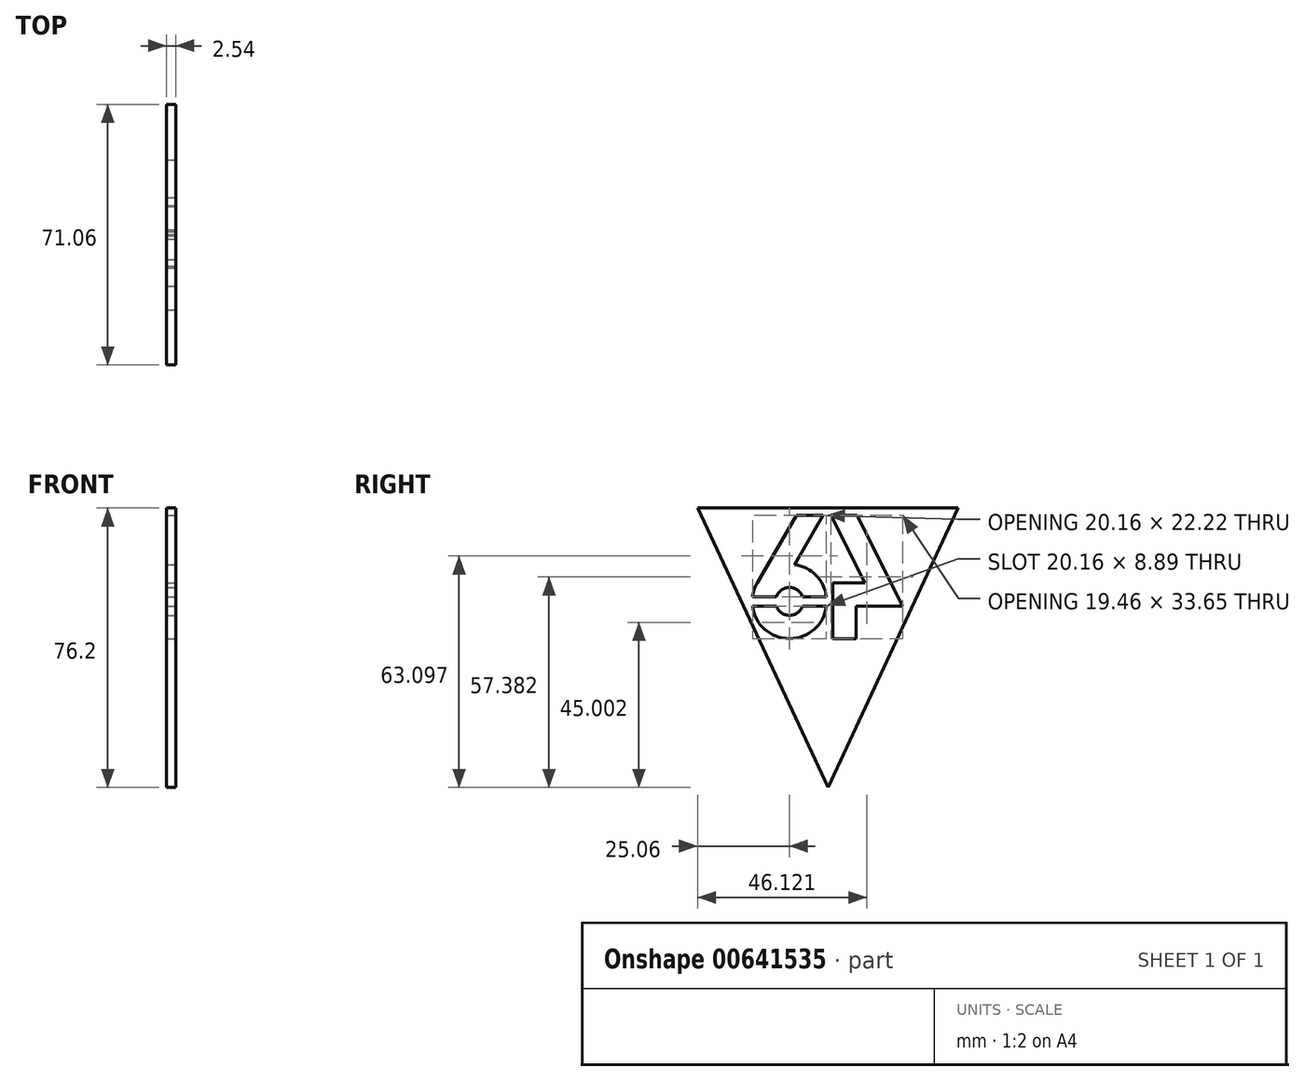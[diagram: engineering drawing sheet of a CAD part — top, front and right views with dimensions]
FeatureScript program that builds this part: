
annotation { "Feature Type Name" : "Feature", "Feature Type Description" : "" }
export const myFeature = defineFeature(function(context is Context, id is Id, definition is map)
    precondition{}
    {
        {
            var Q0;
            Q0=qCreatedBy(makeId("Right.planeOp"),FACE);
            var sketch = newSketch(context, id + "F0", { "sketchPlane" : qUnion([Q0])});
            skLineSegment(sketch, "E0", {"start": v(-35.53, 0) * mm, "end": v(35.53, 0) * mm});
            skLineSegment(sketch, "E1", {"start": v(35.53, 0) * mm, "end": v(0, -76.2) * mm});
            skLineSegment(sketch, "E2", {"start": v(0, -76.2) * mm, "end": v(-35.53, 0) * mm});
            skLineSegment(sketch, "E3", {"start": v(0, -76.2) * mm, "end": v(0, 0) * mm});
            skLineSegment(sketch, "E4", {"start": v(-8.62, -2) * mm, "end": v(-1.29, -2) * mm});
            skLineSegment(sketch, "E5", {"start": v(-1.29, -2) * mm, "end": v(-9.05, -15.42) * mm});
            skLineSegment(sketch, "E6", {"start": v(-8.62, -2) * mm, "end": v(-19.26, -20.4) * mm});
            skArc(sketch, "E7", {"start": v(-19.26, -20.4) * mm, "mid": v(-20.1, -22.24) * mm, "end": v(-20.55, -24.21) * mm});
            skLineSegment(sketch, "E8", {"start": v(7.96, -2) * mm, "end": v(20.32, -26.75) * mm});
            skLineSegment(sketch, "E9", {"start": v(20.32, -26.75) * mm, "end": v(7.62, -26.75) * mm});
            skLineSegment(sketch, "E10", {"start": v(7.62, -26.75) * mm, "end": v(7.62, -35.64) * mm});
            skLineSegment(sketch, "E11", {"start": v(7.62, -35.64) * mm, "end": v(1.27, -35.64) * mm});
            skLineSegment(sketch, "E12", {"start": v(1.27, -35.64) * mm, "end": v(1.27, -20.4) * mm});
            skLineSegment(sketch, "E13", {"start": v(1.27, -20.4) * mm, "end": v(10.05, -20.4) * mm});
            skLineSegment(sketch, "E14", {"start": v(10.05, -20.4) * mm, "end": v(0.86, -2) * mm});
            skLineSegment(sketch, "E15", {"start": v(0.86, -2) * mm, "end": v(7.96, -2) * mm});
            skArc(sketch, "E16", {"start": v(-14.06, -26.75) * mm, "mid": v(-10.47, -29.3) * mm, "end": v(-6.88, -26.75) * mm});
            skLineSegment(sketch, "E17", {"start": v(-14.06, -24.21) * mm, "end": v(-20.55, -24.21) * mm});
            skLineSegment(sketch, "E18", {"start": v(-14.06, -26.75) * mm, "end": v(-20.55, -26.75) * mm});
            skLineSegment(sketch, "E19", {"start": v(-6.88, -24.21) * mm, "end": v(-0.39, -24.21) * mm});
            skLineSegment(sketch, "E20", {"start": v(-6.88, -26.75) * mm, "end": v(-0.39, -26.75) * mm});
            skArc(sketch, "E21.trimOffspring", {"start": v(-20.55, -26.75) * mm, "mid": v(-10.47, -35.64) * mm, "end": v(-0.39, -26.75) * mm});
            skArc(sketch, "E22.trimOffspring", {"start": v(-6.88, -24.21) * mm, "mid": v(-10.47, -21.67) * mm, "end": v(-14.06, -24.21) * mm});
            skArc(sketch, "E23.trimOffspring", {"start": v(-0.39, -24.21) * mm, "mid": v(-3.23, -18.35) * mm, "end": v(-9.05, -15.42) * mm});
            skSolve(sketch);
        }
        {
            var Q0;
            {var subQ1=sQuery(id+"F0.wireOp",EDGE,"E2");Q0=makeQuery(id+"F0.imprint","IMPRINT",FACE,{"disambiguationData":[TD([[makeQuery(id+"F0.imprint","IMPRINT",EDGE,{"derivedFrom":subQ1}),-1.0]])]});}
            var Q1;
            {var subQ0=sQuery(id+"F0.wireOp",EDGE,"E1");Q1=makeQuery(id+"F0.imprint","IMPRINT",FACE,{"disambiguationData":[TD([[makeQuery(id+"F0.imprint","IMPRINT",EDGE,{"derivedFrom":subQ0}),-1.0]])]});}
            extrude(context, id + "F1", {"entities" : qUnion([Q0, Q1]), "oppositeDirection" : true, "depth" : 2.54 * mm, "offsetDistance" : 25.4 * mm});
        }
    });
